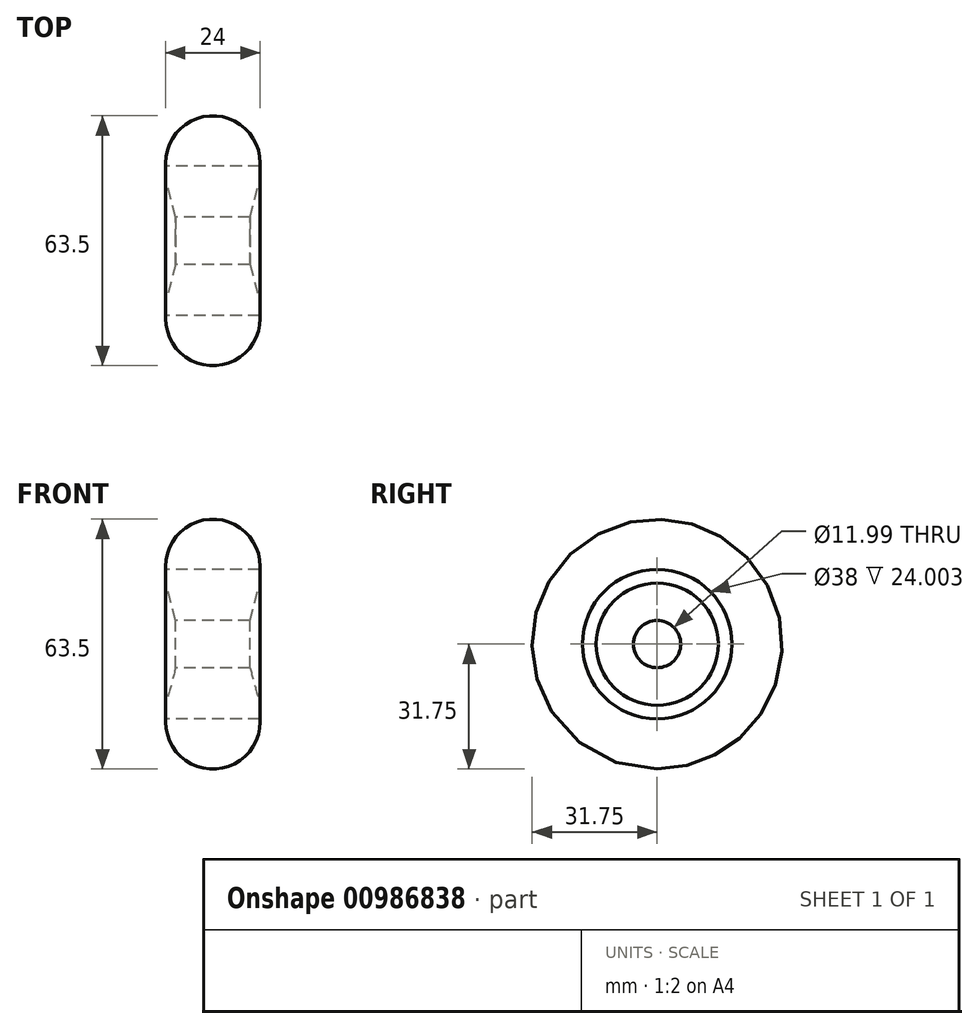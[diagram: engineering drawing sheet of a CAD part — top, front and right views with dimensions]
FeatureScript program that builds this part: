
annotation { "Feature Type Name" : "Feature", "Feature Type Description" : "" }
export const myFeature = defineFeature(function(context is Context, id is Id, definition is map)
    precondition{}
    {
        {
            var Q0;
            Q0=qCreatedBy(makeId("Right.planeOp"),FACE);
            var sketch = newSketch(context, id + "F0", { "sketchPlane" : qUnion([Q0])});
            skCircle(sketch, "E0", {"center": v(0, 0) * mm, "radius": 31.75 * mm});
            skCircle(sketch, "E1", {"center": v(0, 0) * mm, "radius": 19 * mm});
            skCircle(sketch, "E2", {"center": v(0, 0) * mm, "radius": 16 * mm});
            skCircle(sketch, "E3", {"center": v(0, 0) * mm, "radius": 6 * mm});
            skSolve(sketch);
        }
        {
            var Q0;
            Q0=makeQuery(id+"F0.imprint","IMPRINT",FACE,{"disambiguationData":[TD([[makeQuery(id+"F0.imprint","IMPRINT",EDGE,{"derivedFrom":sQuery(id+"F0.wireOp",EDGE,"E0")}),1.0]])]});
            extrude(context, id + "F1", {"entities" : qUnion([Q0]), "depth" : 24 * mm, "offsetDistance" : 25.4 * mm});
        }
        {
            var Q0;
            Q0=makeQuery(id+"F1.opExtrude","CAP_EDGE",EDGE,{"disambiguationData":[OSD([sQuery(id+"F0.wireOp",EDGE,"E0")])],"isStart":false});
            var Q1;
            Q1=makeQuery(id+"F1.opExtrude","CAP_EDGE",EDGE,{"disambiguationData":[OSD([sQuery(id+"F0.wireOp",EDGE,"E0")])],"isStart":true});
            fillet(context, id + "F2", {"entities" : qUnion([Q0, Q1]), "radius" : 12 * mm, "tangentPropagation" : true, "allowEdgeOverflow" : false});
        }
        {
            var Q0;
            Q0=makeQuery(id+"F0.imprint","IMPRINT",FACE,{"disambiguationData":[TD([[makeQuery(id+"F0.imprint","IMPRINT",EDGE,{"derivedFrom":sQuery(id+"F0.wireOp",EDGE,"E1")}),1.0]])]});
            extrude(context, id + "F3", {"entities" : qUnion([Q0]), "depth" : 24 * mm, "offsetDistance" : 25.4 * mm});
        }
        {
            var Q0;
            Q0=makeQuery(id+"F0.imprint","IMPRINT",FACE,{"disambiguationData":[TD([[makeQuery(id+"F0.imprint","IMPRINT",EDGE,{"derivedFrom":sQuery(id+"F0.wireOp",EDGE,"E2")}),1.0]])]});
            extrude(context, id + "F4", {"entities" : qUnion([Q0]), "operationType" : NewBodyOperationType.ADD, "depth" : 24 * mm, "offsetDistance" : 25.4 * mm});
        }
        {
            var Q0;
            Q0=makeQuery(id+"F4.opExtrude","CAP_EDGE",EDGE,{"disambiguationData":[OSD([sQuery(id+"F0.wireOp",EDGE,"E3")])],"isStart":false});
            chamfer(context, id + "F5", {"entities" : qUnion([Q0]), "chamferType" : ChamferType.OFFSET_ANGLE, "width" : 9.52 * mm, "oppositeDirection" : true, "angle" : 15 * degree, "tangentPropagation" : true});
        }
        {
            var Q0;
            Q0=makeQuery(id+"F4.opExtrude","CAP_EDGE",EDGE,{"disambiguationData":[OSD([sQuery(id+"F0.wireOp",EDGE,"E3")])],"isStart":true});
            chamfer(context, id + "F6", {"entities" : qUnion([Q0]), "chamferType" : ChamferType.OFFSET_ANGLE, "width" : 9.52 * mm, "oppositeDirection" : false, "angle" : 15 * degree, "tangentPropagation" : true});
        }
    });
